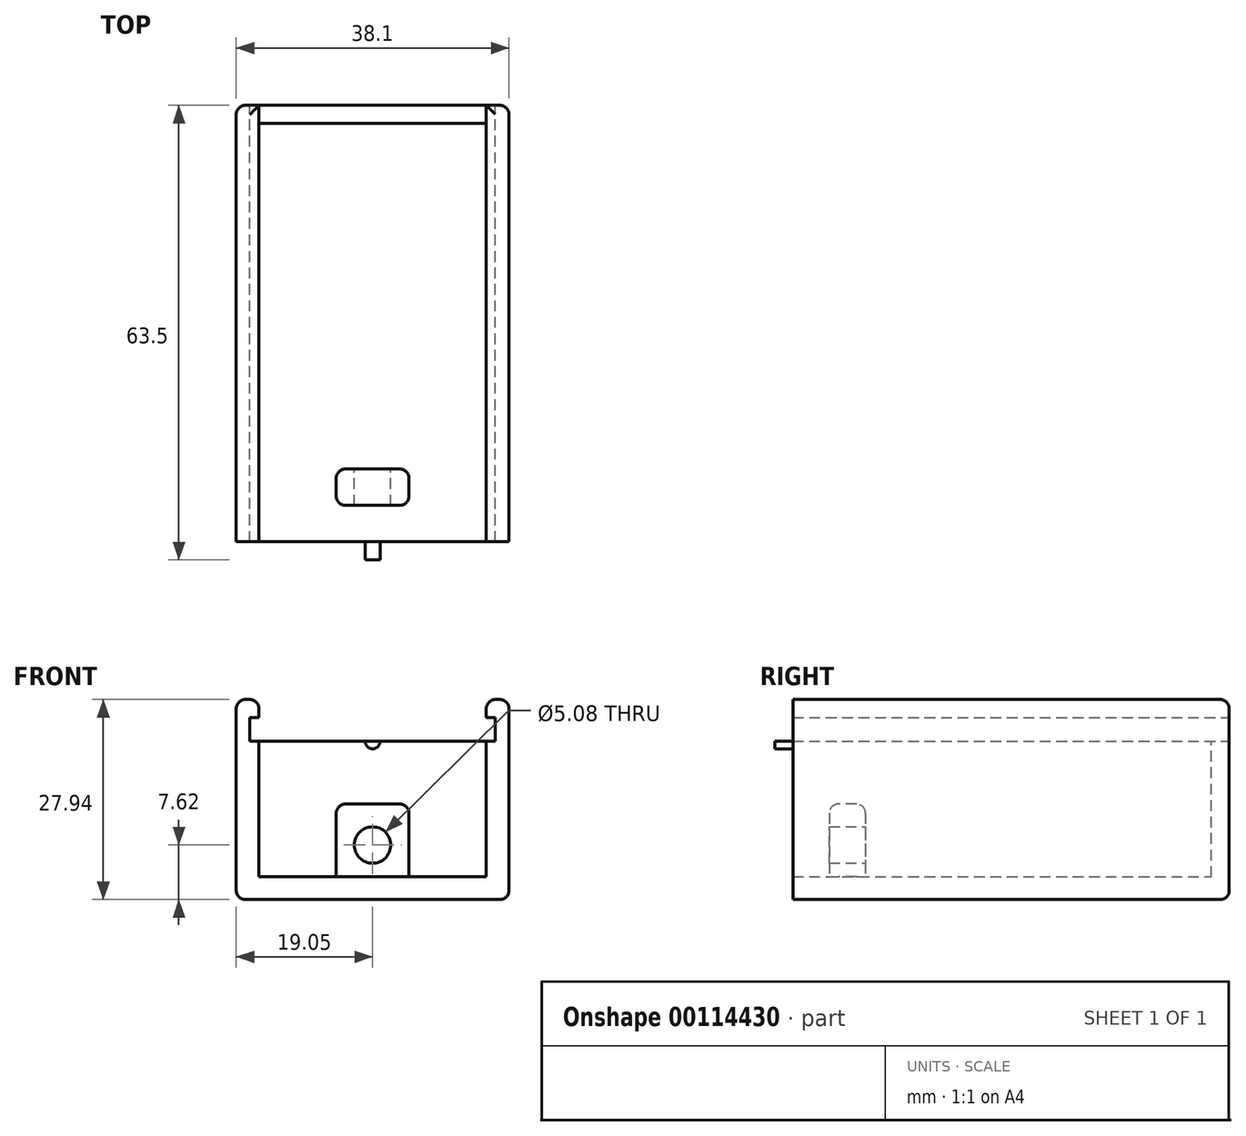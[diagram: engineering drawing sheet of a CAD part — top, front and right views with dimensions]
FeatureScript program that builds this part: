
annotation { "Feature Type Name" : "Feature", "Feature Type Description" : "" }
export const myFeature = defineFeature(function(context is Context, id is Id, definition is map)
    precondition{}
    {
        {
            var Q0;
            Q0=qCreatedBy(makeId("Front.planeOp"),FACE);
            var sketch = newSketch(context, id + "F0", { "sketchPlane" : qUnion([Q0])});
            skLineSegment(sketch, "E0.bottom", {"start": v(19.05, -13.97) * mm, "end": v(-19.05, -13.97) * mm});
            skLineSegment(sketch, "E0.top", {"start": v(19.05, 13.97) * mm, "end": v(15.88, 13.97) * mm});
            skLineSegment(sketch, "E0.left", {"start": v(19.05, -13.97) * mm, "end": v(19.05, 13.97) * mm});
            skLineSegment(sketch, "E0.right", {"start": v(-19.05, -13.97) * mm, "end": v(-19.05, 13.97) * mm});
            skPoint(sketch, "E0.middle", {"position": v(0, 0) * mm});
            skLineSegment(sketch, "E1", {"start": v(-15.88, 13.97) * mm, "end": v(-15.88, 11.43) * mm});
            skLineSegment(sketch, "E2", {"start": v(-15.88, 11.43) * mm, "end": v(-17.15, 11.43) * mm});
            skLineSegment(sketch, "E3", {"start": v(-17.15, 11.43) * mm, "end": v(-17.15, 8.13) * mm});
            skLineSegment(sketch, "E4", {"start": v(-17.15, 8.13) * mm, "end": v(-15.88, 8.13) * mm});
            skLineSegment(sketch, "E5", {"start": v(-15.88, 8.13) * mm, "end": v(-15.87, -10.8) * mm});
            skLineSegment(sketch, "E6", {"start": v(-15.87, -10.8) * mm, "end": v(0, -10.8) * mm});
            skLineSegment(sketch, "E7.MirrorCS", {"start": v(15.88, 11.43) * mm, "end": v(17.15, 11.43) * mm});
            skLineSegment(sketch, "E8.MirrorCS", {"start": v(17.15, 8.13) * mm, "end": v(15.88, 8.13) * mm});
            skLineSegment(sketch, "E9.MirrorCS", {"start": v(15.88, 13.97) * mm, "end": v(15.88, 11.43) * mm});
            skLineSegment(sketch, "E10.MirrorCS", {"start": v(17.15, 11.43) * mm, "end": v(17.15, 8.13) * mm});
            skLineSegment(sketch, "E11.MirrorCS", {"start": v(15.87, 8.13) * mm, "end": v(15.87, -10.8) * mm});
            skLineSegment(sketch, "E12.MirrorCS", {"start": v(15.87, -10.8) * mm, "end": v(0, -10.8) * mm});
            skLineSegment(sketch, "E13.trimOffspring", {"start": v(-15.88, 13.97) * mm, "end": v(-19.05, 13.97) * mm});
            skSolve(sketch);
        }
        {
            var Q0;
            Q0=makeQuery(id+"F0.imprint","IMPRINT",FACE,{"disambiguationData":[TD([[makeQuery(id+"F0.imprint","IMPRINT",EDGE,{"derivedFrom":sQuery(id+"F0.wireOp",EDGE,"E0.bottom")}),-1.0]])]});
            extrude(context, id + "F1", {"entities" : qUnion([Q0]), "endBound" : BoundingType.SYMMETRIC, "depth" : 63.5 * mm});
        }
        {
            var Q0;
            Q0=makeQuery(id+"F1.opExtrude","SWEPT_FACE",FACE,{"disambiguationData":[OSD([sQuery(id+"F0.wireOp",EDGE,"E11.MirrorCS")])]});
            var sketch = newSketch(context, id + "F2", { "sketchPlane" : qUnion([Q0])});
            skLineSegment(sketch, "E14.bottom", {"start": v(31.75, 8.13) * mm, "end": v(29.2, 8.13) * mm});
            skLineSegment(sketch, "E14.top", {"start": v(31.75, -10.8) * mm, "end": v(29.2, -10.8) * mm});
            skLineSegment(sketch, "E14.left", {"start": v(31.75, 8.13) * mm, "end": v(31.75, -10.8) * mm});
            skLineSegment(sketch, "E14.right", {"start": v(29.2, 8.13) * mm, "end": v(29.21, -10.8) * mm});
            skLineSegment(sketch, "E15.MirrorCS", {"start": v(-29.2, 8.13) * mm, "end": v(-29.2, -10.8) * mm});
            skLineSegment(sketch, "E16.MirrorCS", {"start": v(-31.75, 8.13) * mm, "end": v(-31.75, -10.8) * mm});
            skLineSegment(sketch, "E17.MirrorCS", {"start": v(-31.75, -10.8) * mm, "end": v(-29.2, -10.8) * mm});
            skLineSegment(sketch, "E18.MirrorCS", {"start": v(-31.75, 8.13) * mm, "end": v(-29.2, 8.13) * mm});
            skSolve(sketch);
        }
        {
            var Q0;
            Q0=makeQuery(id+"F2.imprint","IMPRINT",FACE,{"disambiguationData":[TD([[makeQuery(id+"F2.imprint","IMPRINT",EDGE,{"derivedFrom":sQuery(id+"F2.wireOp",EDGE,"E15.MirrorCS")}),-1.0]])]});
            var Q1;
            Q1=makeQuery(id+"F2.imprint","IMPRINT",FACE,{"disambiguationData":[TD([[makeQuery(id+"F2.imprint","IMPRINT",EDGE,{"derivedFrom":sQuery(id+"F2.wireOp",EDGE,"E14.bottom")}),1.0]])]});
            var Q2;
            Q2=makeQuery(id+"F1.opExtrude","SWEPT_FACE",FACE,{"disambiguationData":[OSD([sQuery(id+"F0.wireOp",EDGE,"E5")])]});
            extrude(context, id + "F3", {"entities" : qUnion([Q0, Q1]), "operationType" : NewBodyOperationType.ADD, "endBound" : BoundingType.UP_TO_SURFACE, "endBoundEntityFace" : qUnion([Q2]), "depth" : 25.4 * mm});
        }
        {
            var Q0;
            Q0=makeQuery(id+"F3.boolean.opBoolean","MERGE",FACE,{"derivedFrom":[makeQuery(id+"F1.opExtrude","CAP_FACE",FACE,{"disambiguationData":[OSD([sQuery(id+"F0.wireOp",EDGE,"E0.bottom"),sQuery(id+"F0.wireOp",EDGE,"E0.top"),sQuery(id+"F0.wireOp",EDGE,"E0.left"),sQuery(id+"F0.wireOp",EDGE,"E0.right"),sQuery(id+"F0.wireOp",EDGE,"E1"),sQuery(id+"F0.wireOp",EDGE,"E2"),sQuery(id+"F0.wireOp",EDGE,"E3"),sQuery(id+"F0.wireOp",EDGE,"E4"),sQuery(id+"F0.wireOp",EDGE,"E5"),sQuery(id+"F0.wireOp",EDGE,"E6"),sQuery(id+"F0.wireOp",EDGE,"E7.MirrorCS"),sQuery(id+"F0.wireOp",EDGE,"E8.MirrorCS"),sQuery(id+"F0.wireOp",EDGE,"E9.MirrorCS"),sQuery(id+"F0.wireOp",EDGE,"E10.MirrorCS"),sQuery(id+"F0.wireOp",EDGE,"E11.MirrorCS"),sQuery(id+"F0.wireOp",EDGE,"E12.MirrorCS"),sQuery(id+"F0.wireOp",EDGE,"E13.trimOffspring")])],"isStart":false}),makeQuery(id+"F3.opExtrude","SWEPT_FACE",FACE,{"disambiguationData":[OSD([sQuery(id+"F2.wireOp",EDGE,"E14.left")])]})]});
            var sketch = newSketch(context, id + "F4", { "sketchPlane" : qUnion([Q0])});
            skArc(sketch, "E19", {"start": v(1.03, 8.13) * mm, "mid": v(0, 7.1) * mm, "end": v(-1.03, 8.13) * mm});
            skSolve(sketch);
        }
        {
            var Q0;
            {var subQ0=sQuery(id+"F4.wireOp",EDGE,"E19");Q0=makeQuery(id+"F4.imprint","IMPRINT",FACE,{"disambiguationData":[TD([[makeQuery(id+"F4.imprint","IMPRINT",EDGE,{"derivedFrom":subQ0}),-1.0]])]});}
            var Q1;
            Q1=makeQuery(id+"F3.opExtrude","SWEPT_FACE",FACE,{"disambiguationData":[OSD([sQuery(id+"F2.wireOp",EDGE,"E14.right")])]});
            extrude(context, id + "F5", {"entities" : qUnion([Q0]), "operationType" : NewBodyOperationType.REMOVE, "endBound" : BoundingType.UP_TO_SURFACE, "oppositeDirection" : true, "endBoundEntityFace" : qUnion([Q1]), "depth" : 25.4 * mm});
        }
        {
            var Q0;
            Q0=makeQuery(id+"F1.opExtrude","SWEPT_FACE",FACE,{"disambiguationData":[OSD([sQuery(id+"F0.wireOp",EDGE,"E6"),sQuery(id+"F0.wireOp",EDGE,"E12.MirrorCS")])]});
            var sketch = newSketch(context, id + "F6", { "sketchPlane" : qUnion([Q0])});
            skLineSegment(sketch, "E20.bottom", {"start": v(5.08, -19.05) * mm, "end": v(-5.08, -19.05) * mm});
            skLineSegment(sketch, "E20.top", {"start": v(5.08, -24.13) * mm, "end": v(-5.08, -24.13) * mm});
            skLineSegment(sketch, "E20.left", {"start": v(5.08, -19.05) * mm, "end": v(5.08, -24.13) * mm});
            skLineSegment(sketch, "E20.right", {"start": v(-5.08, -19.05) * mm, "end": v(-5.08, -24.13) * mm});
            skPoint(sketch, "E20.middle", {"position": v(0, -21.59) * mm});
            skSolve(sketch);
        }
        {
            var Q0;
            Q0=makeQuery(id+"F6.imprint","IMPRINT",FACE,{"disambiguationData":[TD([[makeQuery(id+"F6.imprint","IMPRINT",EDGE,{"derivedFrom":sQuery(id+"F6.wireOp",EDGE,"E20.bottom")}),1.0]])]});
            extrude(context, id + "F7", {"entities" : qUnion([Q0]), "operationType" : NewBodyOperationType.ADD, "depth" : 10.16 * mm});
        }
        {
            var Q0;
            Q0=makeQuery(id+"F1.opExtrude","CAP_EDGE",EDGE,{"disambiguationData":[OSD([sQuery(id+"F0.wireOp",EDGE,"E0.left")])],"isStart":true});
            var Q1;
            Q1=makeQuery(id+"F1.opExtrude","SWEPT_EDGE",EDGE,{"disambiguationData":[OSD([sQuery(id+"F0.wireOp",EDGE,"E0.top"),sQuery(id+"F0.wireOp",EDGE,"E0.left")])]});
            var Q2;
            Q2=makeQuery(id+"F1.opExtrude","CAP_EDGE",EDGE,{"disambiguationData":[OSD([sQuery(id+"F0.wireOp",EDGE,"E0.left")])],"isStart":false});
            var Q3;
            Q3=makeQuery(id+"F1.opExtrude","SWEPT_EDGE",EDGE,{"disambiguationData":[OSD([sQuery(id+"F0.wireOp",EDGE,"E0.bottom"),sQuery(id+"F0.wireOp",EDGE,"E0.left")])]});
            var Q4;
            Q4=makeQuery(id+"F1.opExtrude","CAP_EDGE",EDGE,{"disambiguationData":[OSD([sQuery(id+"F0.wireOp",EDGE,"E0.bottom")])],"isStart":false});
            var Q5;
            Q5=makeQuery(id+"F1.opExtrude","CAP_EDGE",EDGE,{"disambiguationData":[OSD([sQuery(id+"F0.wireOp",EDGE,"E0.right")])],"isStart":false});
            var Q6;
            Q6=makeQuery(id+"F1.opExtrude","SWEPT_EDGE",EDGE,{"disambiguationData":[OSD([sQuery(id+"F0.wireOp",EDGE,"E0.right"),sQuery(id+"F0.wireOp",EDGE,"E13.trimOffspring")])]});
            var Q7;
            Q7=makeQuery(id+"F1.opExtrude","CAP_EDGE",EDGE,{"disambiguationData":[OSD([sQuery(id+"F0.wireOp",EDGE,"E0.right")])],"isStart":true});
            var Q8;
            Q8=makeQuery(id+"F1.opExtrude","SWEPT_EDGE",EDGE,{"disambiguationData":[OSD([sQuery(id+"F0.wireOp",EDGE,"E0.bottom"),sQuery(id+"F0.wireOp",EDGE,"E0.right")])]});
            var Q9;
            Q9=makeQuery(id+"F1.opExtrude","CAP_EDGE",EDGE,{"disambiguationData":[OSD([sQuery(id+"F0.wireOp",EDGE,"E0.bottom")])],"isStart":true});
            var Q10;
            Q10=makeQuery(id+"F7.opExtrude","CAP_EDGE",EDGE,{"disambiguationData":[OSD([sQuery(id+"F6.wireOp",EDGE,"E20.bottom")])],"isStart":false});
            var Q11;
            Q11=makeQuery(id+"F7.opExtrude","CAP_EDGE",EDGE,{"disambiguationData":[OSD([sQuery(id+"F6.wireOp",EDGE,"E20.right")])],"isStart":false});
            var Q12;
            Q12=makeQuery(id+"F7.opExtrude","SWEPT_EDGE",EDGE,{"disambiguationData":[OSD([sQuery(id+"F6.wireOp",EDGE,"E20.bottom"),sQuery(id+"F6.wireOp",EDGE,"E20.right")])]});
            var Q13;
            Q13=makeQuery(id+"F7.opExtrude","CAP_EDGE",EDGE,{"disambiguationData":[OSD([sQuery(id+"F6.wireOp",EDGE,"E20.top")])],"isStart":false});
            var Q14;
            Q14=makeQuery(id+"F7.opExtrude","CAP_FACE",FACE,{"disambiguationData":[OSD([sQuery(id+"F6.wireOp",EDGE,"E20.bottom"),sQuery(id+"F6.wireOp",EDGE,"E20.top"),sQuery(id+"F6.wireOp",EDGE,"E20.left"),sQuery(id+"F6.wireOp",EDGE,"E20.right")])],"isStart":false});
            var Q15;
            Q15=makeQuery(id+"F7.opExtrude","SWEPT_EDGE",EDGE,{"disambiguationData":[OSD([sQuery(id+"F6.wireOp",EDGE,"E20.top"),sQuery(id+"F6.wireOp",EDGE,"E20.left")])]});
            var Q16;
            Q16=makeQuery(id+"F7.opExtrude","SWEPT_EDGE",EDGE,{"disambiguationData":[OSD([sQuery(id+"F6.wireOp",EDGE,"E20.bottom"),sQuery(id+"F6.wireOp",EDGE,"E20.left")])]});
            var Q17;
            Q17=makeQuery(id+"F7.opExtrude","SWEPT_EDGE",EDGE,{"disambiguationData":[OSD([sQuery(id+"F6.wireOp",EDGE,"E20.top"),sQuery(id+"F6.wireOp",EDGE,"E20.right")])]});
            var Q18;
            Q18=makeQuery(id+"F1.opExtrude","SWEPT_EDGE",EDGE,{"disambiguationData":[OSD([sQuery(id+"F0.wireOp",EDGE,"E1"),sQuery(id+"F0.wireOp",EDGE,"E13.trimOffspring")])]});
            var Q19;
            Q19=makeQuery(id+"F1.opExtrude","SWEPT_EDGE",EDGE,{"disambiguationData":[OSD([sQuery(id+"F0.wireOp",EDGE,"E0.top"),sQuery(id+"F0.wireOp",EDGE,"E9.MirrorCS")])]});
            var Q20;
            Q20=makeQuery(id+"F1.opExtrude","CAP_EDGE",EDGE,{"disambiguationData":[OSD([sQuery(id+"F0.wireOp",EDGE,"E0.top")])],"isStart":false});
            var Q21;
            Q21=makeQuery(id+"F1.opExtrude","CAP_EDGE",EDGE,{"disambiguationData":[OSD([sQuery(id+"F0.wireOp",EDGE,"E13.trimOffspring")])],"isStart":false});
            var Q22;
            Q22=makeQuery(id+"F1.opExtrude","CAP_EDGE",EDGE,{"disambiguationData":[OSD([sQuery(id+"F0.wireOp",EDGE,"E13.trimOffspring")])],"isStart":true});
            var Q23;
            Q23=makeQuery(id+"F1.opExtrude","CAP_EDGE",EDGE,{"disambiguationData":[OSD([sQuery(id+"F0.wireOp",EDGE,"E0.top")])],"isStart":true});
            fillet(context, id + "F8", {"entities" : qUnion([Q0, Q1, Q2, Q3, Q4, Q5, Q6, Q7, Q8, Q9, Q10, Q11, Q12, Q13, Q14, Q15, Q16, Q17, Q18, Q19, Q20, Q21, Q22, Q23]), "radius" : 1.27 * mm, "tangentPropagation" : true, "allowEdgeOverflow" : false});
        }
        {
            var Q0;
            Q0=makeQuery(id+"F7.opExtrude","SWEPT_FACE",FACE,{"disambiguationData":[OSD([sQuery(id+"F6.wireOp",EDGE,"E20.bottom")])]});
            var sketch = newSketch(context, id + "F9", { "sketchPlane" : qUnion([Q0])});
            skCircle(sketch, "E21", {"center": v(0, -6.35) * mm, "radius": 2.54 * mm});
            skPoint(sketch, "E21.centerSnap0", {"position": v(-3.8, -6.35) * mm});
            skSolve(sketch);
        }
        {
            var Q0;
            Q0=makeQuery(id+"F9.imprint","IMPRINT",FACE,{"disambiguationData":[TD([[makeQuery(id+"F9.imprint","IMPRINT",EDGE,{"derivedFrom":sQuery(id+"F9.wireOp",EDGE,"E21")}),1.0]])]});
            var Q1;
            Q1=makeQuery(id+"F7.opExtrude","SWEPT_FACE",FACE,{"disambiguationData":[OSD([sQuery(id+"F6.wireOp",EDGE,"E20.top")])]});
            extrude(context, id + "F10", {"entities" : qUnion([Q0]), "operationType" : NewBodyOperationType.REMOVE, "endBound" : BoundingType.UP_TO_SURFACE, "oppositeDirection" : true, "endBoundEntityFace" : qUnion([Q1]), "depth" : 25.4 * mm});
        }
    });
